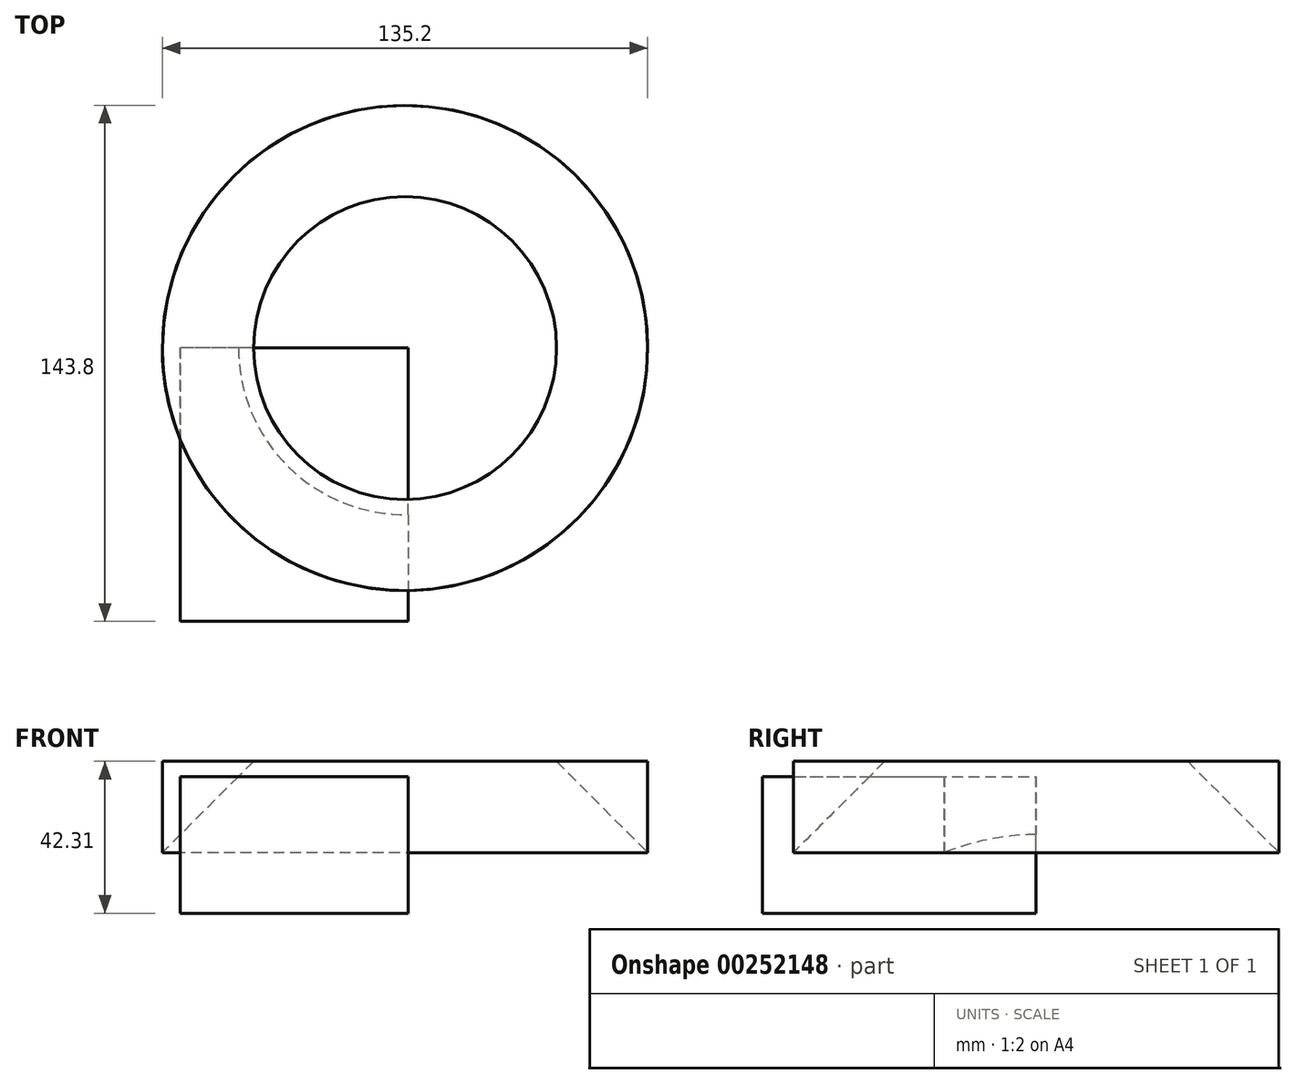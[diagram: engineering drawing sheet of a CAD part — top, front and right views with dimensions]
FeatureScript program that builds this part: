
annotation { "Feature Type Name" : "Feature", "Feature Type Description" : "" }
export const myFeature = defineFeature(function(context is Context, id is Id, definition is map)
    precondition{}
    {
        {
            var Q0;
            Q0=qCreatedBy(makeId("Front.planeOp"),FACE);
            var sketch = newSketch(context, id + "F0", { "sketchPlane" : qUnion([Q0])});
            skLineSegment(sketch, "E0.bottom", {"start": v(0.92, 14.92) * mm, "end": v(-62.58, 14.92) * mm});
            skLineSegment(sketch, "E0.top", {"start": v(0.92, 53.02) * mm, "end": v(-62.58, 53.02) * mm});
            skLineSegment(sketch, "E0.left", {"start": v(0.92, 14.92) * mm, "end": v(0.92, 53.02) * mm});
            skLineSegment(sketch, "E0.right", {"start": v(-62.58, 14.92) * mm, "end": v(-62.58, 53.02) * mm});
            skSolve(sketch);
        }
        {
            var Q0;
            Q0 = qSketchRegion(id + "F0", true);
            extrude(context, id + "F1", {"entities" : qUnion([Q0]), "depth" : 76.2 * mm});
        }
        {
            var Q0;
            Q0=qCreatedBy(makeId("Front.planeOp"),FACE);
            var sketch = newSketch(context, id + "F2", { "sketchPlane" : qUnion([Q0])});
            skLineSegment(sketch, "E1", {"start": v(-67.6, 31.82) * mm, "end": v(-42.2, 57.23) * mm});
            skLineSegment(sketch, "E2", {"start": v(-42.2, 57.23) * mm, "end": v(-67.6, 57.23) * mm});
            skLineSegment(sketch, "E3", {"start": v(-67.6, 57.23) * mm, "end": v(-67.6, 31.82) * mm});
            skCircle(sketch, "E4", {"center": v(-28.39, -27.19) * mm, "radius": 12.3 * mm});
            skLineSegment(sketch, "E5", {"start": v(0, -17.96) * mm, "end": v(0, -60.33) * mm, "construction": true});
            skSolve(sketch);
        }
        {
            var Q0;
            Q0=makeQuery(id+"F2.imprint","IMPRINT",FACE,{"disambiguationData":[TD([[makeQuery(id+"F2.imprint","IMPRINT",EDGE,{"derivedFrom":sQuery(id+"F2.wireOp",EDGE,"E1")}),1.0]])]});
            var Q1;
            Q1=sQuery(id+"F2.wireOp",EDGE,"E5");
            revolve(context, id + "F3", {"operationType" : NewBodyOperationType.ADD, "entities" : qUnion([Q0]), "axis" : qUnion([Q1]), "revolveType" : RevolveType.FULL});
        }
    });
